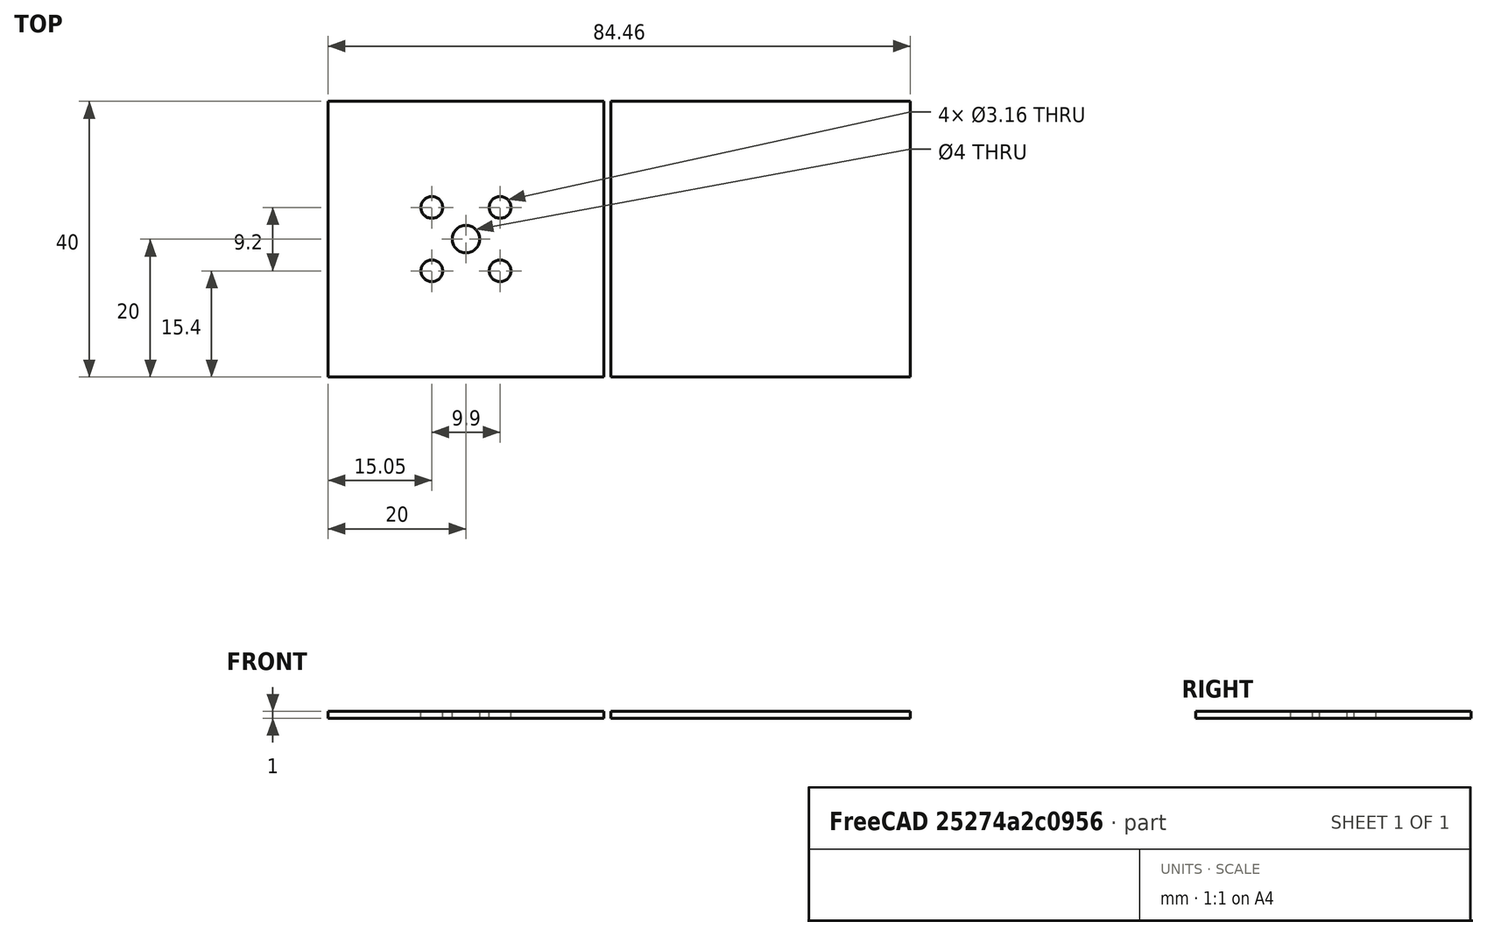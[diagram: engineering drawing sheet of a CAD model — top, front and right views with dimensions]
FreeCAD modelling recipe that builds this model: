
FCSTD DOCUMENT  (FreeCAD 0.16R)
Label: PanelKit
License: All rights reserved
LicenseURL: http://en.wikipedia.org/wiki/All_rights_reserved
objects: Part::Cylinder×5, Part::Cut×5, Part::Box×2
note: 12 computed .brp shape members not serialized (recipe doc carries the construction recipe); baked Part::Feature solids carry a one-line shape summary decoded from their .brp

FEATURE [Part::Box] Box  label="Cube"
  Height = 1
  Length = 40
  Placement = pos=(-20,-20,0) rot=(0,0,1;0rad)
  Width = 40
FEATURE [Part::Cylinder] Cylinder
  Angle = 360
  Height = 1
  Placement = pos=(-4.95,-4.6,0) rot=(0,0,1;0rad)
  Radius = 1.58
FEATURE [Part::Cylinder] Cylinder001
  Angle = 360
  Height = 1
  Placement = pos=(-4.95,4.6,0) rot=(0,0,1;0rad)
  Radius = 1.58
FEATURE [Part::Cylinder] Cylinder002
  Angle = 360
  Height = 1
  Placement = pos=(4.95,4.6,0) rot=(0,0,1;0rad)
  Radius = 1.58
FEATURE [Part::Cylinder] Cylinder003
  Angle = 360
  Height = 1
  Placement = pos=(4.95,-4.6,0) rot=(0,0,1;0rad)
  Radius = 1.58
FEATURE [Part::Cylinder] Cylinder004
  Angle = 360
  Height = 1
  Radius = 2
FEATURE [Part::Box] Box001  label="Cube001"
  Height = 1
  Length = 43.46
  Placement = pos=(21,-20,0) rot=(0,0,1;0rad)
  Width = 40
FEATURE [Part::Cut] Cut
  Base = -> Box
  Tool = -> Cylinder002
FEATURE [Part::Cut] Cut001
  Base = -> Cut
  Tool = -> Cylinder001
FEATURE [Part::Cut] Cut002
  Base = -> Cut001
  Tool = -> Cylinder
FEATURE [Part::Cut] Cut003
  Base = -> Cut002
  Tool = -> Cylinder003
FEATURE [Part::Cut] Cut004
  Base = -> Cut003
  Tool = -> Cylinder004
